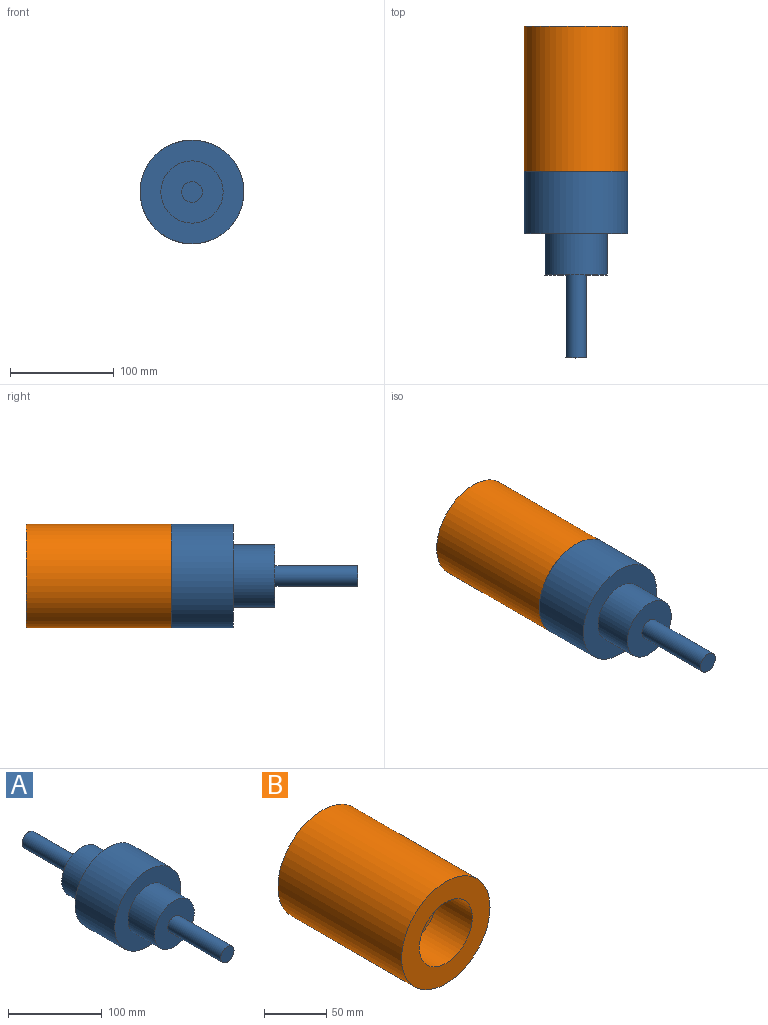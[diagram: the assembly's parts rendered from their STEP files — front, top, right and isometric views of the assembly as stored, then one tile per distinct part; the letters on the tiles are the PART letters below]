
ASSEMBLY  parts=2 mates=1
PART A: 11 faces, bbox 100x300x100 mm
  f0: cylinder r=50mm len=100mm, axis (0,1,0), area 18849.6mm2, adj f1,f2
  f1: plane 100x100mm, normal (0,-1,0), area 5026.5mm2, adj f0,f5
  f2: plane 100x100mm, normal (0,1,0), area 5026.5mm2, adj f0,f3
  f3: cylinder r=30mm len=60mm, axis (0,-1,0), area 7539.8mm2, adj f2,f4
  f4: plane 60x60mm, normal (0,1,0), area 2513.3mm2, adj f3,f9
  f5: cylinder r=30mm len=60mm, axis (0,1,0), area 7539.8mm2, adj f1,f6
  f6: plane 60x60mm, normal (0,-1,0), area 2513.3mm2, adj f5,f7
  f7: cylinder r=10mm len=80mm, axis (0,1,0), area 5026.5mm2, adj f6,f8
  f8: plane 20x20mm, normal (0,-1,0), area 314.2mm2, adj f7
  f9: cylinder r=10mm len=80mm, axis (0,-1,0), area 5026.5mm2, adj f4,f10
  f10: plane 20x20mm, normal (0,1,0), area 314.2mm2, adj f9
PART B: 7 faces, bbox 100x140x100 mm
  f0: cylinder r=50mm len=140mm, axis (0,1,0), area 43982.3mm2, adj f1,f2
  f1: plane 100x100mm, normal (0,-1,0), area 5026.5mm2, adj f0,f3
  f2: plane 100x100mm, normal (0,1,0), area 7854mm2, adj f0
  f3: cylinder r=30mm len=60mm, axis (0,-1,0), area 7539.8mm2, adj f1,f4
  f4: plane 60x60mm, normal (0,-1,0), area 2531.3mm2, adj f3,f5
  f5: cylinder r=9.71mm len=80mm, axis (0,-1,0), area 4880.2mm2, adj f4,f6
  f6: plane 19.42x19.42mm, normal (0,-1,0), area 296.1mm2, adj f5
PLACE A t=(707.3,130.08,448.31)mm
PLACE B t=(707.3,300.08,448.31)mm
MATE fastened B.f0 <-> A.f0  axis (0,-1,0) through (707.3,160.08,448.31)mm
